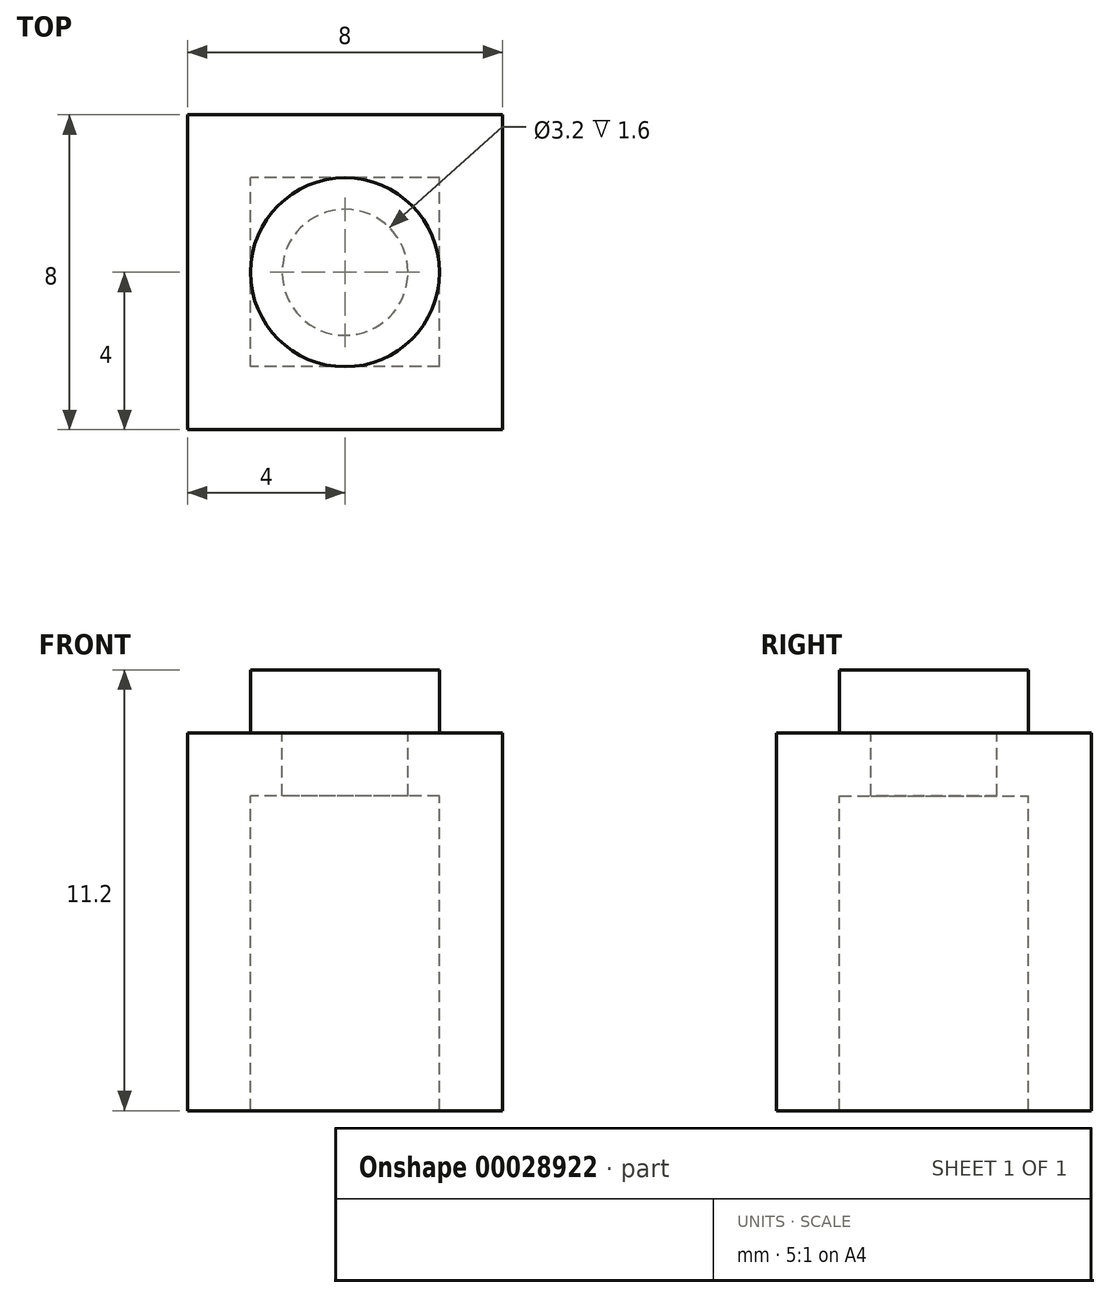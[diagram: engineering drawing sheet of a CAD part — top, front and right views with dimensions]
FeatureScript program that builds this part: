
annotation { "Feature Type Name" : "Feature", "Feature Type Description" : "" }
export const myFeature = defineFeature(function(context is Context, id is Id, definition is map)
    precondition{}
    {
        {
            var Q0;
            Q0=qCreatedBy(makeId("Top.planeOp"),FACE);
            var sketch = newSketch(context, id + "F0", { "sketchPlane" : qUnion([Q0])});
            skLineSegment(sketch, "E0.rect.bottom", {"start": v(4, -4) * mm, "end": v(-4, -4) * mm});
            skLineSegment(sketch, "E0.rect.top", {"start": v(4, 4) * mm, "end": v(-4, 4) * mm});
            skLineSegment(sketch, "E0.rect.left", {"start": v(4, -4) * mm, "end": v(4, 4) * mm});
            skLineSegment(sketch, "E0.rect.right", {"start": v(-4, -4) * mm, "end": v(-4, 4) * mm});
            skPoint(sketch, "E0.rect.middle", {"position": v(0, 0) * mm});
            skLineSegment(sketch, "E1.0", {"start": v(2.4, 2.4) * mm, "end": v(-2.4, 2.4) * mm});
            skLineSegment(sketch, "E1.1", {"start": v(2.4, -2.4) * mm, "end": v(2.4, 2.4) * mm});
            skLineSegment(sketch, "E1.2", {"start": v(2.4, -2.4) * mm, "end": v(-2.4, -2.4) * mm});
            skLineSegment(sketch, "E1.3", {"start": v(-2.4, -2.4) * mm, "end": v(-2.4, 2.4) * mm});
            skCircle(sketch, "E2", {"center": v(0, 0) * mm, "radius": 2.4 * mm});
            skCircle(sketch, "E3", {"center": v(0, 0) * mm, "radius": 1.6 * mm});
            skSolve(sketch);
        }
        {
            var Q0;
            Q0=makeQuery(id+"F0.imprint","IMPRINT",FACE,{"disambiguationData":[TD([[makeQuery(id+"F0.imprint","IMPRINT",EDGE,{"derivedFrom":sQuery(id+"F0.wireOp",EDGE,"E3")}),1.0]])]});
            var Q1;
            Q1=makeQuery(id+"F0.imprint","IMPRINT",FACE,{"disambiguationData":[TD([[makeQuery(id+"F0.imprint","IMPRINT",EDGE,{"derivedFrom":sQuery(id+"F0.wireOp",EDGE,"E3")}),-1.0]])]});
            extrude(context, id + "F1", {"entities" : qUnion([Q0, Q1]), "depth" : 1.6 * mm});
        }
        {
            var Q0;
            {var subQ1=sQuery(id+"F0.wireOp",EDGE,"E1.3");var subQ3=sQuery(id+"F0.wireOp",EDGE,"E1.2");var subQ5=makeQuery(id+"F0.imprint","INTERSECT",VERTEX,{"derivedFrom":[subQ3,subQ1]});Q0=makeQuery(id+"F0.imprint","IMPRINT",FACE,{"disambiguationData":[TD([[makeQuery(id+"F0.imprint","IMPRINT",EDGE,{"disambiguationData":[TD([[subQ5,1.0]])],"derivedFrom":subQ3}),-1.0]])]});}
            var Q1;
            {var subQ1=sQuery(id+"F0.wireOp",EDGE,"E1.3");var subQ3=sQuery(id+"F0.wireOp",EDGE,"E1.0");var subQ5=makeQuery(id+"F0.imprint","INTERSECT",VERTEX,{"derivedFrom":[subQ3,subQ1]});Q1=makeQuery(id+"F0.imprint","IMPRINT",FACE,{"disambiguationData":[TD([[makeQuery(id+"F0.imprint","IMPRINT",EDGE,{"disambiguationData":[TD([[subQ5,1.0]])],"derivedFrom":subQ3}),1.0]])]});}
            var Q2;
            {var subQ1=sQuery(id+"F0.wireOp",EDGE,"E1.1");var subQ3=sQuery(id+"F0.wireOp",EDGE,"E1.0");var subQ5=makeQuery(id+"F0.imprint","INTERSECT",VERTEX,{"derivedFrom":[subQ3,subQ1]});Q2=makeQuery(id+"F0.imprint","IMPRINT",FACE,{"disambiguationData":[TD([[makeQuery(id+"F0.imprint","IMPRINT",EDGE,{"disambiguationData":[TD([[subQ5,-1.0]])],"derivedFrom":subQ3}),1.0]])]});}
            var Q3;
            {var subQ1=sQuery(id+"F0.wireOp",EDGE,"E1.2");var subQ3=sQuery(id+"F0.wireOp",EDGE,"E1.1");var subQ5=makeQuery(id+"F0.imprint","INTERSECT",VERTEX,{"derivedFrom":[subQ3,subQ1]});Q3=makeQuery(id+"F0.imprint","IMPRINT",FACE,{"disambiguationData":[TD([[makeQuery(id+"F0.imprint","IMPRINT",EDGE,{"disambiguationData":[TD([[subQ5,-1.0]])],"derivedFrom":subQ3}),1.0]])]});}
            var Q4;
            Q4=makeQuery(id+"F1.opExtrude","CAP_FACE",FACE,{"disambiguationData":[OSD([sQuery(id+"F0.wireOp",EDGE,"E2")])],"isStart":false});
            var Q5;
            Q5=makeQuery(id+"F0.imprint","IMPRINT",FACE,{"disambiguationData":[TD([[makeQuery(id+"F0.imprint","IMPRINT",EDGE,{"derivedFrom":sQuery(id+"F0.wireOp",EDGE,"E3")}),-1.0]])]});
            extrude(context, id + "F2", {"entities" : qUnion([Q0, Q1, Q2, Q3, Q4, Q5]), "operationType" : NewBodyOperationType.ADD, "oppositeDirection" : true, "depth" : 1.6 * mm});
        }
        {
            var Q0;
            Q0=makeQuery(id+"F0.imprint","IMPRINT",FACE,{"disambiguationData":[TD([[makeQuery(id+"F0.imprint","IMPRINT",EDGE,{"derivedFrom":sQuery(id+"F0.wireOp",EDGE,"E0.rect.bottom")}),-1.0]])]});
            extrude(context, id + "F3", {"entities" : qUnion([Q0]), "operationType" : NewBodyOperationType.ADD, "oppositeDirection" : true, "depth" : 9.6 * mm});
        }
    });
